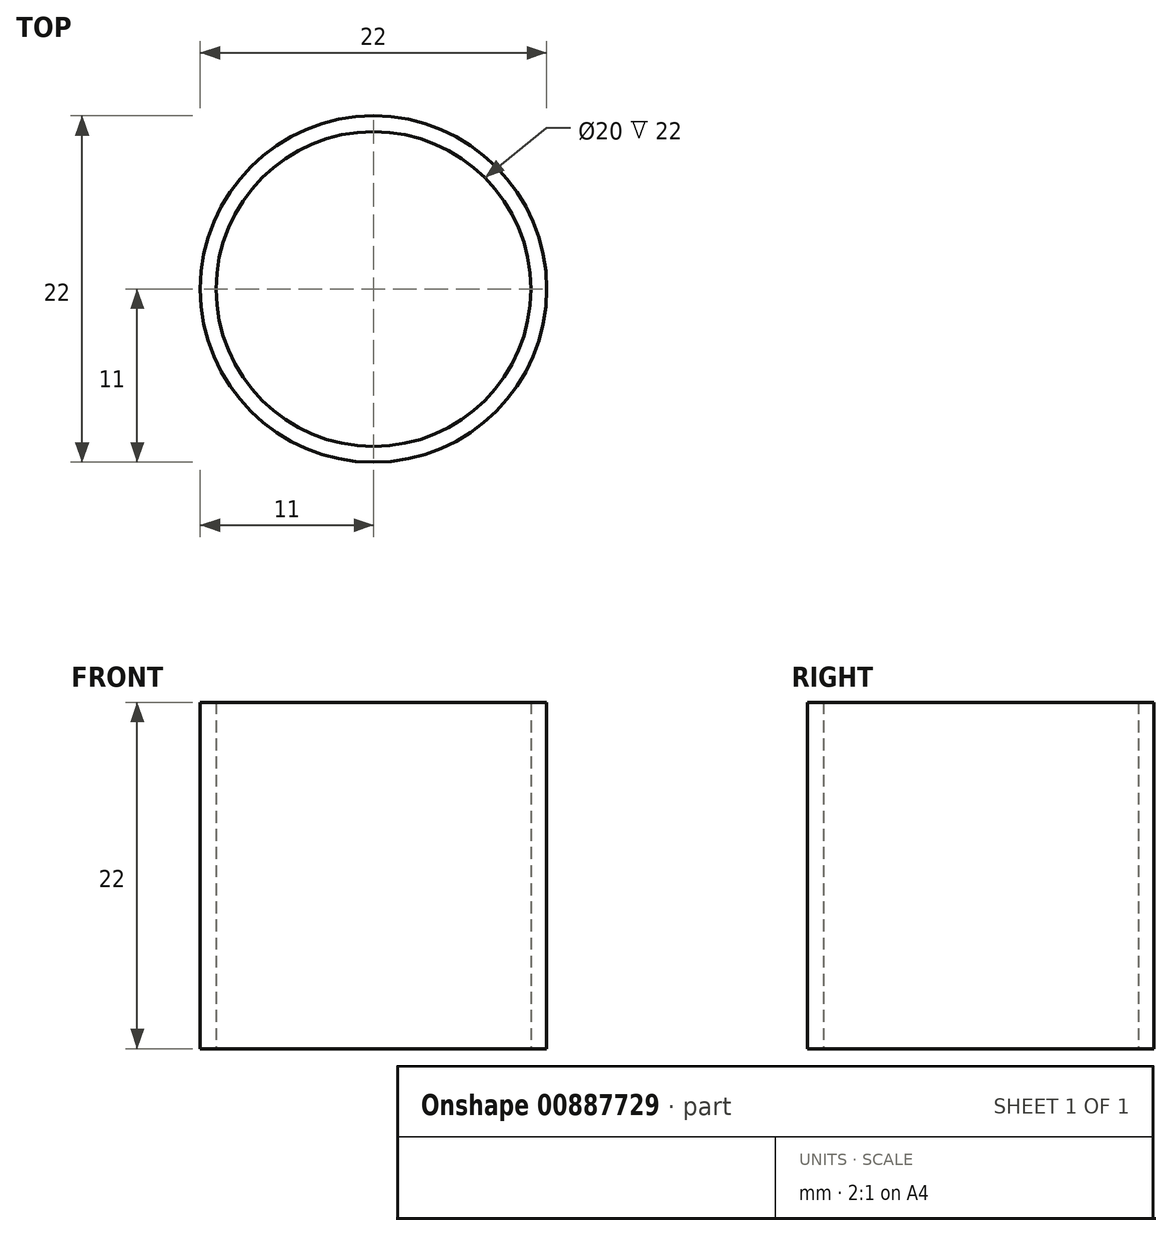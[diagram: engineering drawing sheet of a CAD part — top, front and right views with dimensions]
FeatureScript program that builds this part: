
annotation { "Feature Type Name" : "Feature", "Feature Type Description" : "" }
export const myFeature = defineFeature(function(context is Context, id is Id, definition is map)
    precondition{}
    {
        {
            var Q0;
            Q0=qCreatedBy(makeId("Top.planeOp"),FACE);
            var sketch = newSketch(context, id + "F0", { "sketchPlane" : qUnion([Q0])});
            skCircle(sketch, "E0", {"center": v(0, 0) * mm, "radius": 11 * mm});
            skCircle(sketch, "E1", {"center": v(0, 0) * mm, "radius": 10 * mm});
            skSolve(sketch);
        }
        {
            var Q0;
            Q0=makeQuery(id+"F0.imprint","IMPRINT",FACE,{"disambiguationData":[TD([[makeQuery(id+"F0.imprint","IMPRINT",EDGE,{"derivedFrom":sQuery(id+"F0.wireOp",EDGE,"E0")}),1.0]])]});
            extrude(context, id + "F1", {"entities" : qUnion([Q0]), "depth" : 22 * mm, "offsetDistance" : 25 * mm});
        }
    });
